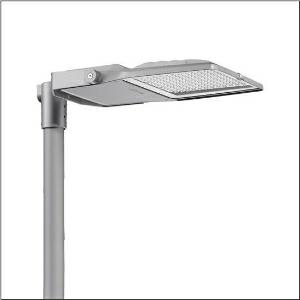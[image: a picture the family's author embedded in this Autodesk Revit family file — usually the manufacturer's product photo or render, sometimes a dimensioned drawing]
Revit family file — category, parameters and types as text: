
# Revit family: floodlight_fl_21_iq_midi___pl33t_5xa7781e2f3a_de32
name_source: partatom
category: Lighting Fixtures
units: mm (PartAtom-declared; Revit-internal decimal feet)

## family parameters
Cut with Voids When Loaded = No
Host = Face
Light Source = No
Part Type = Normal
Room Calculation Point = No
Round Connector Dimension = Use Diameter
Shared = No

## types (1)
- --- (1 x LED, 26540 lm, 208.1 W, 3000K)
    Apparent Load = 208 VA
    CIE Flux Codes = 26 75 99 100 100
    Color Rendering = 70
    Color Temperature = 3000K
    Default Elevation = 1800 mm
    Description = Floodlight FL 21 iQ midi, floodlight, primary light control with lens, of PMMA, primary optical cover: protective disc, of toughened safety glass, transparent, light distribution: PL33T, light emission: direct distribution, installation type: surface-mounted, lamps: LED, High Power LED, rated values: 26.540lm | 208,1W | 127,5lm/W (begin service life); end service life: 26.540lm | 227,1W; at 50% lumin. flux: 13.270lm | 90,1W | 147,3lm/W, colour temperature: 3000K, colour rendering: CRI > 70, light colour: 730, light setting 1 begin service life: 100% | 26.540lm | 208,1W | 127,5lm/W | 3.000K, light setting 1 end service life: 227,1W, further light settings possible, control: optimised constant luminous flux control (CLO 2.0), Desk-Remote (wireless, voltage-free reading and setting of iQ features in the workshop via application-optimized NFC function/RFID function), Light-Fading, Smart-Wire, Night-Set, Lumen-Switch, Temp-Guard, Auto-Match, pre-setting: linear dimming characteristic, with terminal, 6-pole, mains connection: 220..240V, AC, 50/60Hz, luminaire housing, of diecast aluminium, powder-coated, SITECO metallic grey (DB 702S), corrosivity category C5 mid according to DIN EN ISO 12944suitable for swimming poolschlorine-resistant, sealing non-destructively replaceable, please order mast flange separately, mast bracket, of steel, galvanised, powder-coated, SITECO metallic grey (DB 702S), protection rating (complete): IP66, insulation class (complete): insulation class II (safety insulation), certification: CE, ENEC, VDE, protection symbol: D, impact resistance: IK08, permissible operating ambient temperature: -40..+40°C, permissible operating ambient temperature for outdoor applications: -40..+50°C, standard: DIN EN 12944, LABS conformity tested according to VDMA 24364:2018-05, packaging unit: 1 piece

Light Distribution: PL33T
    Height = 76 mm
    Lamp = 1 x LED
    Lamp Light Flux = 26540 lm
    Lamp Power = 208.1 W
    Lamp count = 1
    Length = 657 mm
    Luminous efficacy = 128 lm/W
    Manufacturer = Siteco
    ModVariant = No
    Model = 5XA7781E2F3A
    Number of Poles = 1
    OnlyDefault = Yes
    Power Factor = 1
    Product Name = Floodlight FL 21 iQ midi | PL33T
    Product group = floodlight | pylon annexe
    ProductGroupID = 6201
    Protection Class = Protection class II
    Protection Degree = IP 66
    RLX_Detail_Level = 1
    RLX_Emergency_Light_Flux = 0 lm
    RLX_Emergency_Type = 0
    RLX_Emergency_Type_DB = No
    RlxData = <blob elided: 153761 chars, md5=403b3b1c>
    Socket = socket
    Standby Power = 0 W
    System Light Flux = 26540 lm
    System Power = 208 W
    Type Comments = factory setting: luminous flux: 100 % | dim-lin: 254 | 710 mA
    Type Image = l_1007123.jpg
    URL = http://relux.com
    VarID = @adj_103965
    Voltage = 0 V
    Weight = 0.00 kg
    Width = 442 mm

## geometry (parser evidence)
native form markers: Blend x4, Sweep x15
no freeform markers — native parametric forms only
